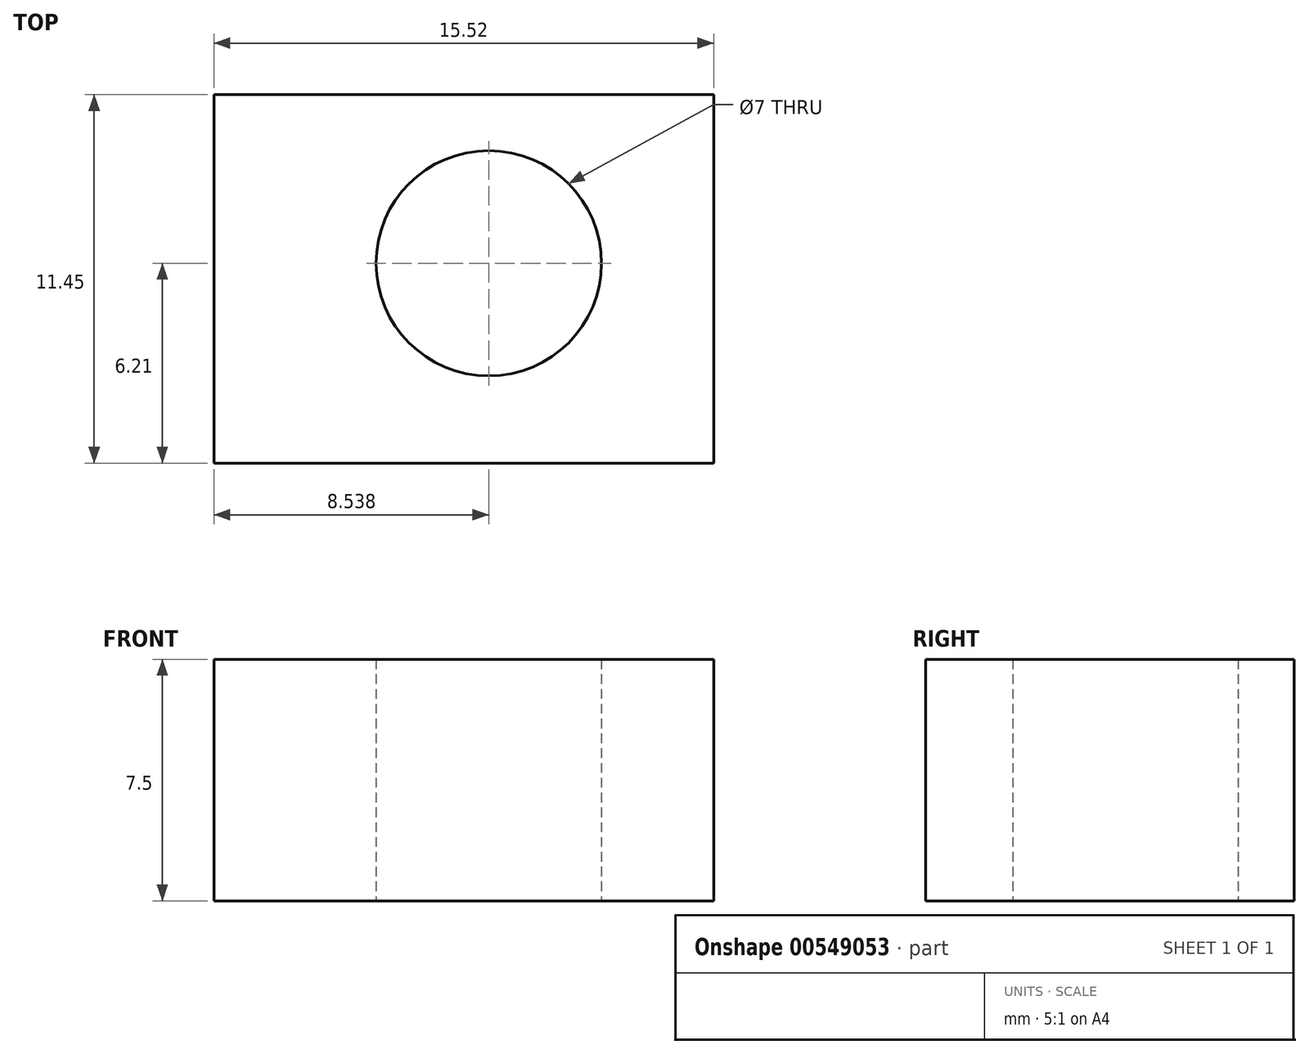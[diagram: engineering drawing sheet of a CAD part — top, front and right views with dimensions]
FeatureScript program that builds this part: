
annotation { "Feature Type Name" : "Feature", "Feature Type Description" : "" }
export const myFeature = defineFeature(function(context is Context, id is Id, definition is map)
    precondition{}
    {
        {
            var Q0;
            Q0=qCreatedBy(makeId("Top.planeOp"),FACE);
            var sketch = newSketch(context, id + "F0", { "sketchPlane" : qUnion([Q0])});
            skCircle(sketch, "E0", {"center": v(-34.33, 24.44) * mm, "radius": 3.5 * mm});
            skLineSegment(sketch, "E1.bottom", {"start": v(-42.87, 29.68) * mm, "end": v(-27.35, 29.68) * mm});
            skLineSegment(sketch, "E1.top", {"start": v(-42.87, 18.23) * mm, "end": v(-27.35, 18.23) * mm});
            skLineSegment(sketch, "E1.left", {"start": v(-42.87, 29.68) * mm, "end": v(-42.87, 18.23) * mm});
            skLineSegment(sketch, "E1.right", {"start": v(-27.35, 29.68) * mm, "end": v(-27.35, 18.23) * mm});
            skSolve(sketch);
        }
        {
            var Q0;
            Q0=makeQuery(id+"F0.imprint","IMPRINT",FACE,{"disambiguationData":[TD([[makeQuery(id+"F0.imprint","IMPRINT",EDGE,{"derivedFrom":sQuery(id+"F0.wireOp",EDGE,"E0")}),-1.0]])]});
            extrude(context, id + "F1", {"entities" : qUnion([Q0]), "endBound" : BoundingType.SYMMETRIC, "depth" : 7.5 * mm, "offsetDistance" : 25 * mm});
        }
    });
